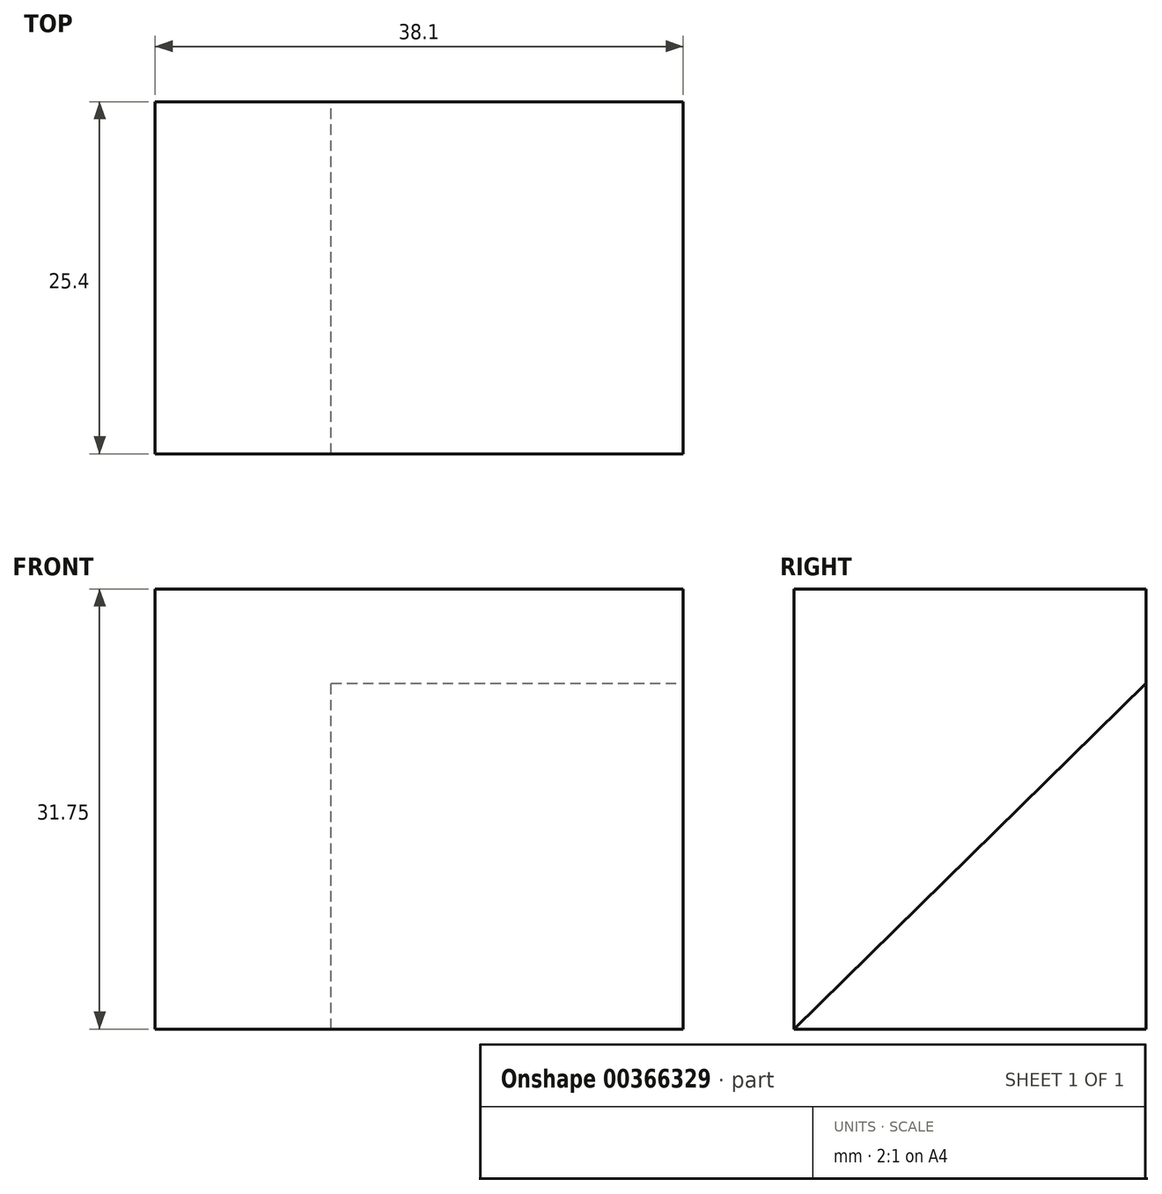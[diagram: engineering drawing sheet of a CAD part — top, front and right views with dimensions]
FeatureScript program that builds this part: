
annotation { "Feature Type Name" : "Feature", "Feature Type Description" : "" }
export const myFeature = defineFeature(function(context is Context, id is Id, definition is map)
    precondition{}
    {
        {
            var Q0;
            Q0=qCreatedBy(makeId("Front.planeOp"),FACE);
            var sketch = newSketch(context, id + "F0", { "sketchPlane" : qUnion([Q0])});
            skLineSegment(sketch, "E0", {"start": v(0, 0) * mm, "end": v(38.1, 0) * mm});
            skLineSegment(sketch, "E1", {"start": v(38.1, 0) * mm, "end": v(38.1, 31.75) * mm});
            skLineSegment(sketch, "E2", {"start": v(38.1, 31.75) * mm, "end": v(0, 31.75) * mm});
            skLineSegment(sketch, "E3", {"start": v(0, 31.75) * mm, "end": v(0, 0) * mm});
            skSolve(sketch);
        }
        {
            var Q0;
            Q0 = qSketchRegion(id + "F0", true);
            extrude(context, id + "F1", {"entities" : qUnion([Q0]), "depth" : 25.4 * mm});
        }
        {
            var Q0;
            Q0=makeQuery(id+"F1.opExtrude","SWEPT_FACE",FACE,{"disambiguationData":[OSD([sQuery(id+"F0.wireOp",EDGE,"E1")])]});
            var sketch = newSketch(context, id + "F2", { "sketchPlane" : qUnion([Q0])});
            skLineSegment(sketch, "E4", {"start": v(-25.4, 0) * mm, "end": v(0, 24.93) * mm});
            skLineSegment(sketch, "E5", {"start": v(0, 24.93) * mm, "end": v(0, 0) * mm});
            skLineSegment(sketch, "E6", {"start": v(0, 0) * mm, "end": v(-25.4, 0) * mm});
            skSolve(sketch);
        }
        {
            var Q0;
            Q0=makeQuery(id+"F2.imprint","IMPRINT",FACE,{"disambiguationData":[TD([[makeQuery(id+"F2.imprint","IMPRINT",EDGE,{"derivedFrom":sQuery(id+"F2.wireOp",EDGE,"E4")}),-1.0]])]});
            extrude(context, id + "F3", {"entities" : qUnion([Q0]), "operationType" : NewBodyOperationType.REMOVE, "oppositeDirection" : true, "depth" : 25.4 * mm});
        }
    });
